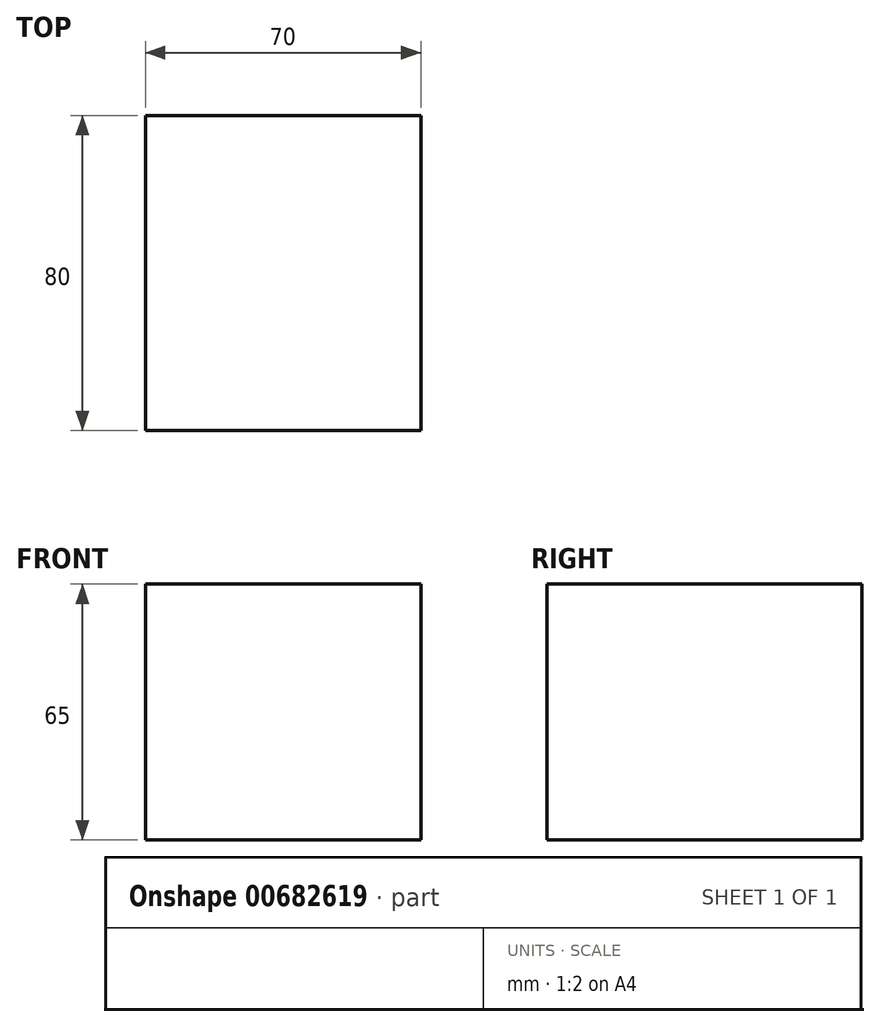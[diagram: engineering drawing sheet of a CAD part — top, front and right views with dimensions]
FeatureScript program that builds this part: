
annotation { "Feature Type Name" : "Feature", "Feature Type Description" : "" }
export const myFeature = defineFeature(function(context is Context, id is Id, definition is map)
    precondition{}
    {
        {
            var Q0;
            Q0=qCreatedBy(makeId("Right.planeOp"),FACE);
            var sketch = newSketch(context, id + "F0", { "sketchPlane" : qUnion([Q0])});
            skLineSegment(sketch, "E0.bottom", {"start": v(40, 32.5) * mm, "end": v(-40, 32.5) * mm});
            skLineSegment(sketch, "E0.top", {"start": v(40, -32.5) * mm, "end": v(-40, -32.5) * mm});
            skLineSegment(sketch, "E0.left", {"start": v(40, 32.5) * mm, "end": v(40, -32.5) * mm});
            skLineSegment(sketch, "E0.right", {"start": v(-40, 32.5) * mm, "end": v(-40, -32.5) * mm});
            skPoint(sketch, "E0.middle", {"position": v(0, 0) * mm});
            skSolve(sketch);
        }
        {
            var Q0;
            Q0=makeQuery(id+"F0.imprint","IMPRINT",FACE,{"disambiguationData":[TD([[makeQuery(id+"F0.imprint","IMPRINT",EDGE,{"derivedFrom":sQuery(id+"F0.wireOp",EDGE,"E0.bottom")}),1.0]])]});
            extrude(context, id + "F1", {"entities" : qUnion([Q0]), "depth" : 35 * mm, "offsetDistance" : 25 * mm, "hasSecondDirection" : true, "secondDirectionOppositeDirection" : true, "secondDirectionDepth" : 35 * mm});
        }
    });
